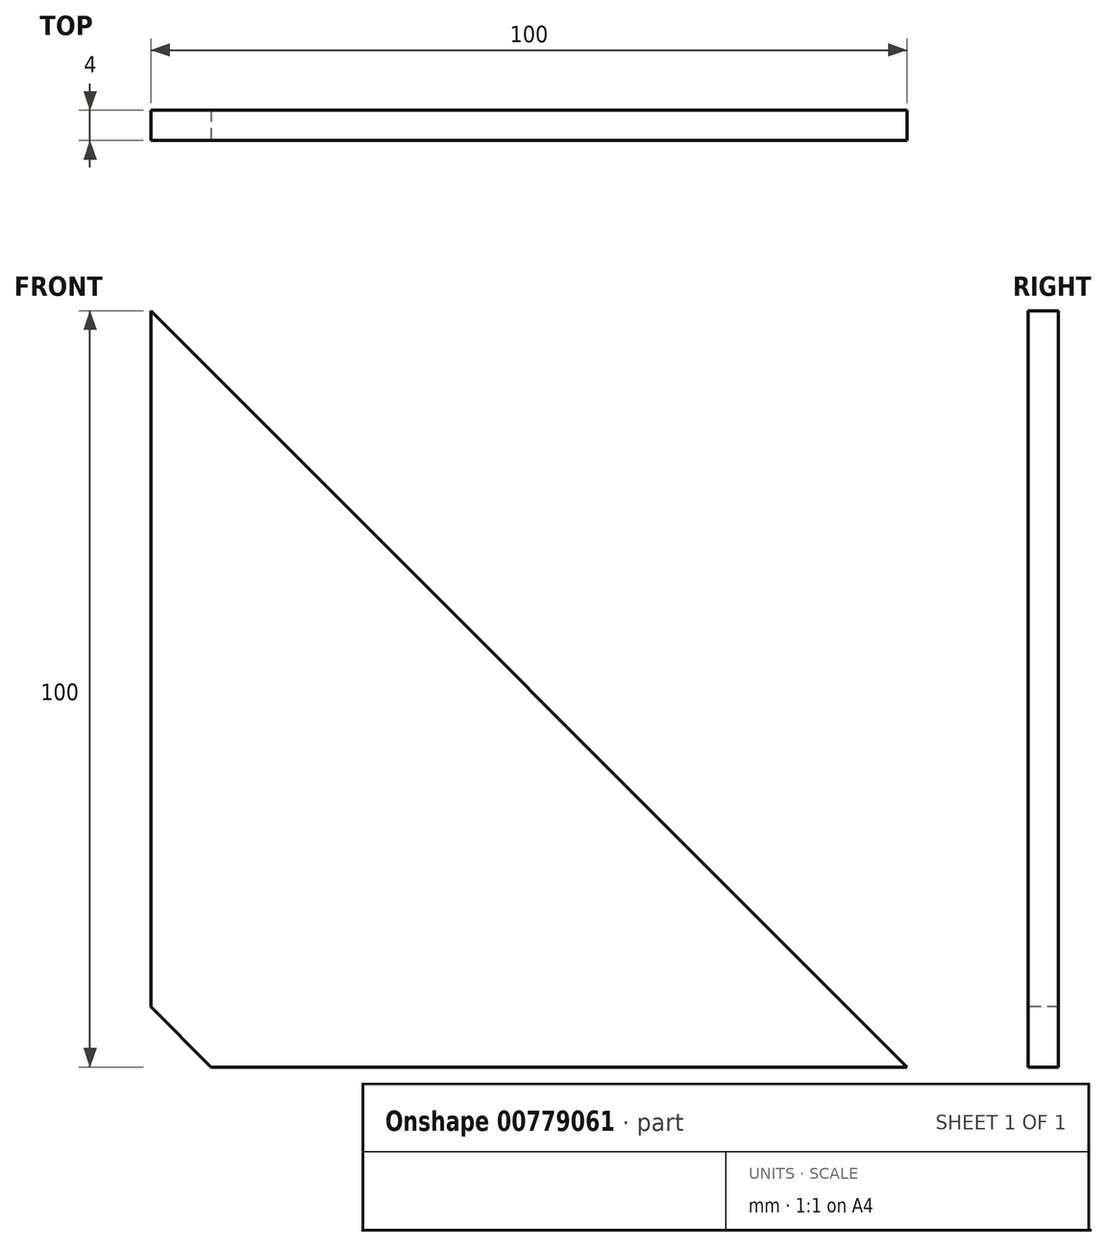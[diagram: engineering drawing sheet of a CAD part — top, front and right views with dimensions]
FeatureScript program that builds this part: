
annotation { "Feature Type Name" : "Feature", "Feature Type Description" : "" }
export const myFeature = defineFeature(function(context is Context, id is Id, definition is map)
    precondition{}
    {
        {
            var Q0;
            Q0=qCreatedBy(makeId("Front.planeOp"),FACE);
            var sketch = newSketch(context, id + "F0", { "sketchPlane" : qUnion([Q0])});
            skLineSegment(sketch, "E0", {"start": v(0, 0) * mm, "end": v(0, 100) * mm});
            skLineSegment(sketch, "E1", {"start": v(0, 0) * mm, "end": v(100, 0) * mm});
            skLineSegment(sketch, "E2", {"start": v(100, 0) * mm, "end": v(0, 100) * mm});
            skLineSegment(sketch, "E3", {"start": v(0, 0) * mm, "end": v(0, 8) * mm});
            skLineSegment(sketch, "E4", {"start": v(0, 8) * mm, "end": v(8, 0) * mm});
            skSolve(sketch);
        }
        {
            var Q0;
            {var subQ0=sQuery(id+"F0.wireOp",EDGE,"E2");Q0=makeQuery(id+"F0.imprint","IMPRINT",FACE,{"disambiguationData":[TD([[makeQuery(id+"F0.imprint","IMPRINT",EDGE,{"derivedFrom":subQ0}),1.0]])]});}
            extrude(context, id + "F1", {"entities" : qUnion([Q0]), "oppositeDirection" : true, "depth" : 4 * mm, "offsetDistance" : 25 * mm});
        }
    });
